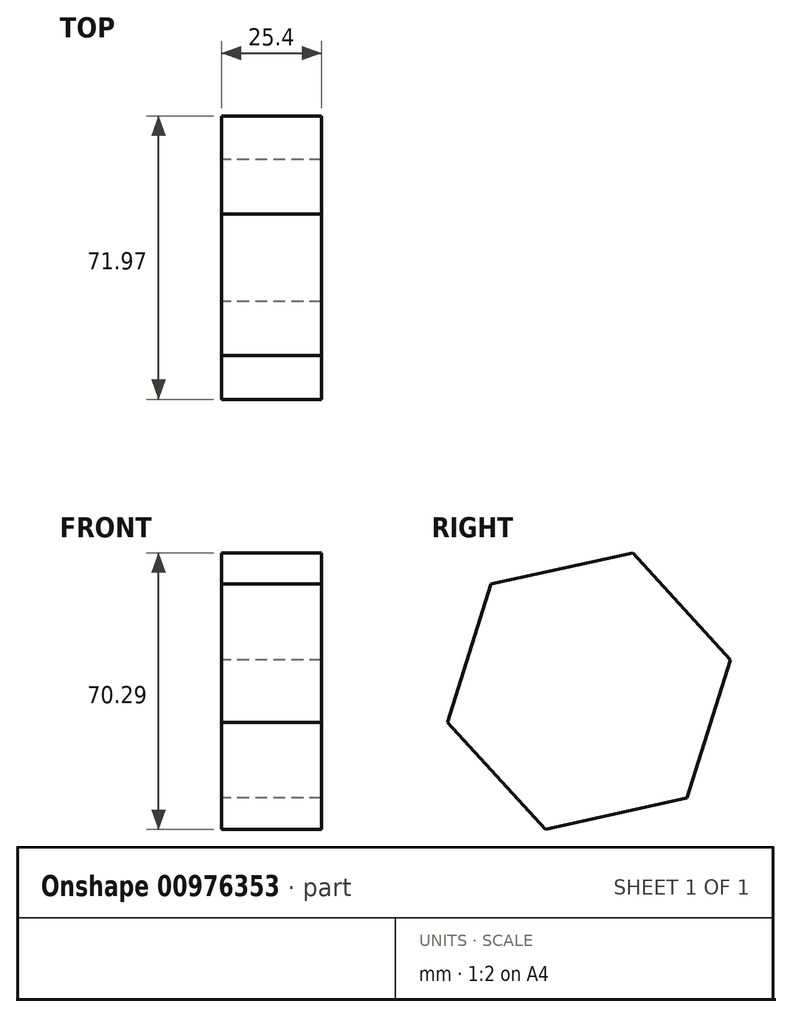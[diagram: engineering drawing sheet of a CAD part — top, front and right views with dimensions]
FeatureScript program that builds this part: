
annotation { "Feature Type Name" : "Feature", "Feature Type Description" : "" }
export const myFeature = defineFeature(function(context is Context, id is Id, definition is map)
    precondition{}
    {
        {
            var Q0;
            Q0=qCreatedBy(makeId("Right.planeOp"),FACE);
            var sketch = newSketch(context, id + "F0", { "sketchPlane" : qUnion([Q0])});
            skCircle(sketch, "E0.cCircle", {"center": v(-20.45, 22.98) * mm, "radius": 36.85 * mm, "construction": true});
            skLineSegment(sketch, "E0.0", {"start": v(4.44, -4.2) * mm, "end": v(-31.54, -12.16) * mm});
            skLineSegment(sketch, "E0.1", {"start": v(-31.54, -12.16) * mm, "end": v(-56.43, 15.02) * mm});
            skLineSegment(sketch, "E0.2", {"start": v(-56.43, 15.02) * mm, "end": v(-45.34, 50.16) * mm});
            skLineSegment(sketch, "E0.3", {"start": v(-45.34, 50.16) * mm, "end": v(-9.36, 58.13) * mm});
            skLineSegment(sketch, "E0.4", {"start": v(-9.36, 58.13) * mm, "end": v(15.54, 30.95) * mm});
            skLineSegment(sketch, "E0.5", {"start": v(15.54, 30.95) * mm, "end": v(4.44, -4.2) * mm});
            skSolve(sketch);
        }
        {
            var Q0;
            Q0 = qSketchRegion(id + "F0", true);
            extrude(context, id + "F1", {"entities" : qUnion([Q0]), "depth" : 25.4 * mm, "offsetDistance" : 25.4 * mm});
        }
    });
